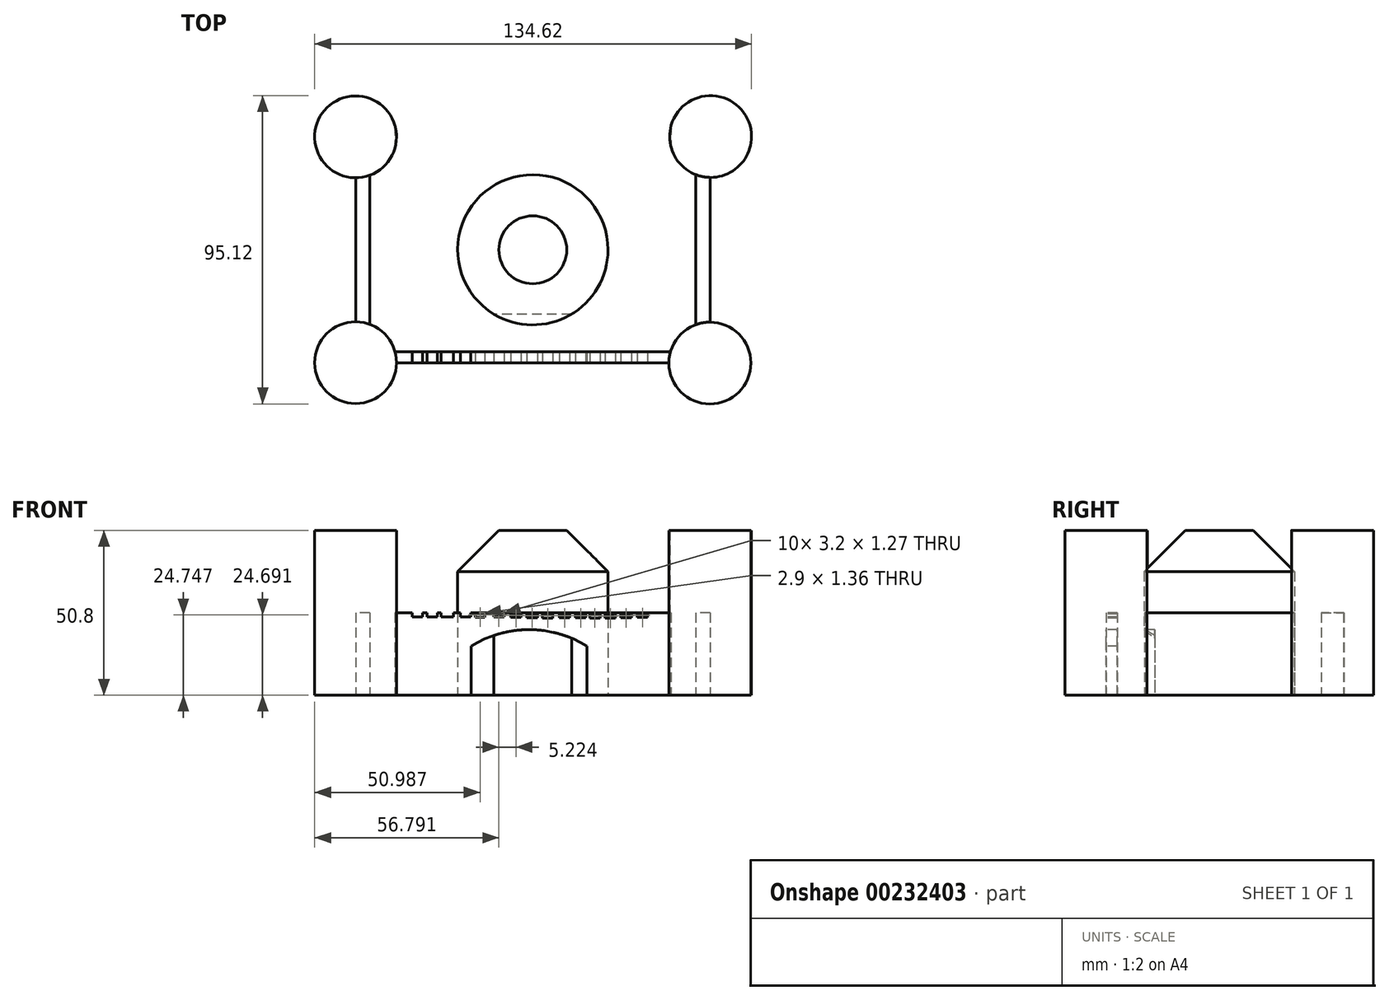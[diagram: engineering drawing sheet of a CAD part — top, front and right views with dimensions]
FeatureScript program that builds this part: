
annotation { "Feature Type Name" : "Feature", "Feature Type Description" : "" }
export const myFeature = defineFeature(function(context is Context, id is Id, definition is map)
    precondition{}
    {
        {
            var Q0;
            Q0=qCreatedBy(makeId("Top.planeOp"),FACE);
            var sketch = newSketch(context, id + "F0", { "sketchPlane" : qUnion([Q0])});
            skLineSegment(sketch, "E0.bottom", {"start": v(41.96, -34.83) * mm, "end": v(-42, -34.83) * mm});
            skLineSegment(sketch, "E0.top", {"start": v(42.17, 34.83) * mm, "end": v(-42, 34.83) * mm});
            skLineSegment(sketch, "E0.left", {"start": v(54.6, -22.32) * mm, "end": v(54.6, 22.32) * mm});
            skLineSegment(sketch, "E0.right", {"start": v(-54.6, -34.83) * mm, "end": v(-54.6, -34.83) * mm});
            skPoint(sketch, "E0.middle", {"position": v(0, 0) * mm});
            skCircle(sketch, "E1", {"center": v(0, 0) * mm, "radius": 23.17 * mm});
            skCircle(sketch, "E2", {"center": v(-54.6, 34.83) * mm, "radius": 12.62 * mm});
            skCircle(sketch, "E3", {"center": v(54.79, 34.94) * mm, "radius": 12.62 * mm});
            skCircle(sketch, "E4", {"center": v(54.58, -34.94) * mm, "radius": 12.62 * mm});
            skCircle(sketch, "E5", {"center": v(-54.6, -34.83) * mm, "radius": 12.62 * mm});
            skLineSegment(sketch, "E6.bottom", {"start": v(42.46, -31.43) * mm, "end": v(-42.46, -31.43) * mm});
            skLineSegment(sketch, "E6.top", {"start": v(42.67, 31.43) * mm, "end": v(-42.46, 31.43) * mm});
            skLineSegment(sketch, "E6.left", {"start": v(50.25, -23.1) * mm, "end": v(50.25, 23.17) * mm});
            skLineSegment(sketch, "E6.right", {"start": v(-50.25, -23) * mm, "end": v(-50.25, 23) * mm});
            skPoint(sketch, "E7.orphan", {"position": v(54.6, 34.83) * mm});
            skLineSegment(sketch, "E8.trimOffspring", {"start": v(-54.6, -22.22) * mm, "end": v(-54.6, 22.22) * mm});
            skPoint(sketch, "E9.orphan", {"position": v(54.6, -34.83) * mm});
            skPoint(sketch, "E10.orphan", {"position": v(50.25, 31.43) * mm});
            skPoint(sketch, "E11.orphan", {"position": v(50.25, -31.43) * mm});
            skPoint(sketch, "E12.orphan", {"position": v(-50.25, -31.43) * mm});
            skPoint(sketch, "E13.orphan", {"position": v(-50.25, 31.43) * mm});
            skPoint(sketch, "E14.left.end.orphan", {"position": v(7.55, 3.82) * mm});
            skPoint(sketch, "E14.bottom.start.orphan", {"position": v(7.55, -3.82) * mm});
            skPoint(sketch, "E14.right.end.orphan", {"position": v(-7.55, 3.82) * mm});
            skPoint(sketch, "E14.right.start.orphan", {"position": v(-7.55, -3.82) * mm});
            skSolve(sketch);
        }
        {
            var Q0;
            {var subQ0=sQuery(id+"F0.wireOp",EDGE,"E0.top");Q0=makeQuery(id+"F0.imprint","IMPRINT",FACE,{"disambiguationData":[TD([[makeQuery(id+"F0.imprint","IMPRINT",EDGE,{"derivedFrom":subQ0}),1.0]])]});}
            var Q1;
            {var subQ0=sQuery(id+"F0.wireOp",EDGE,"E6.right");Q1=makeQuery(id+"F0.imprint","IMPRINT",FACE,{"disambiguationData":[TD([[makeQuery(id+"F0.imprint","IMPRINT",EDGE,{"derivedFrom":subQ0}),1.0]])]});}
            var Q2;
            {var subQ0=sQuery(id+"F0.wireOp",EDGE,"E0.bottom");Q2=makeQuery(id+"F0.imprint","IMPRINT",FACE,{"disambiguationData":[TD([[makeQuery(id+"F0.imprint","IMPRINT",EDGE,{"derivedFrom":subQ0}),-1.0]])]});}
            var Q3;
            {var subQ0=sQuery(id+"F0.wireOp",EDGE,"E0.left");Q3=makeQuery(id+"F0.imprint","IMPRINT",FACE,{"disambiguationData":[TD([[makeQuery(id+"F0.imprint","IMPRINT",EDGE,{"derivedFrom":subQ0}),1.0]])]});}
            extrude(context, id + "F1", {"entities" : qUnion([Q0, Q1, Q2, Q3]), "depth" : 25.4 * mm});
        }
        {
            var Q0;
            {var subQ0=sQuery(id+"F0.wireOp",EDGE,"E2");var subQ1=makeQuery(id+"F0.imprint","INTERSECT",VERTEX,{"derivedFrom":[sQuery(id+"F0.wireOp",EDGE,"E0.top"),subQ0]});Q0=makeQuery(id+"F0.imprint","IMPRINT",FACE,{"disambiguationData":[TD([[makeQuery(id+"F0.imprint","IMPRINT",EDGE,{"disambiguationData":[TD([[subQ1,-1.0]])],"derivedFrom":subQ0}),1.0]])]});}
            var Q1;
            {var subQ0=sQuery(id+"F0.wireOp",EDGE,"E3");var subQ1=makeQuery(id+"F0.imprint","INTERSECT",VERTEX,{"derivedFrom":[sQuery(id+"F0.wireOp",EDGE,"E0.top"),subQ0]});Q1=makeQuery(id+"F0.imprint","IMPRINT",FACE,{"disambiguationData":[TD([[makeQuery(id+"F0.imprint","IMPRINT",EDGE,{"disambiguationData":[TD([[subQ1,-1.0]])],"derivedFrom":subQ0}),1.0]])]});}
            var Q2;
            {var subQ0=sQuery(id+"F0.wireOp",EDGE,"E4");var subQ1=makeQuery(id+"F0.imprint","INTERSECT",VERTEX,{"derivedFrom":[sQuery(id+"F0.wireOp",EDGE,"E0.left"),subQ0]});Q2=makeQuery(id+"F0.imprint","IMPRINT",FACE,{"disambiguationData":[TD([[makeQuery(id+"F0.imprint","IMPRINT",EDGE,{"disambiguationData":[TD([[subQ1,-1.0]])],"derivedFrom":subQ0}),1.0]])]});}
            var Q3;
            {var subQ0=sQuery(id+"F0.wireOp",EDGE,"E5");var subQ1=makeQuery(id+"F0.imprint","INTERSECT",VERTEX,{"derivedFrom":[subQ0,sQuery(id+"F0.wireOp",EDGE,"E6.bottom")]});Q3=makeQuery(id+"F0.imprint","IMPRINT",FACE,{"disambiguationData":[TD([[makeQuery(id+"F0.imprint","IMPRINT",EDGE,{"disambiguationData":[TD([[subQ1,-1.0]])],"derivedFrom":subQ0}),1.0]])]});}
            var Q4;
            Q4=makeQuery(id+"F0.imprint","IMPRINT",FACE,{"disambiguationData":[TD([[makeQuery(id+"F0.imprint","IMPRINT",EDGE,{"derivedFrom":sQuery(id+"F0.wireOp",EDGE,"E1")}),1.0]])]});
            extrude(context, id + "F2", {"entities" : qUnion([Q0, Q1, Q2, Q3, Q4]), "depth" : 50.8 * mm});
        }
        {
            var Q0;
            Q0=makeQuery(id+"F1.opExtrude","SWEPT_FACE",FACE,{"disambiguationData":[OSD([sQuery(id+"F0.wireOp",EDGE,"E0.bottom")])]});
            var sketch = newSketch(context, id + "F3", { "sketchPlane" : qUnion([Q0])});
            skLineSegment(sketch, "E15.bottom", {"start": v(-19.02, 0) * mm, "end": v(16.75, 0) * mm});
            skLineSegment(sketch, "E15.left", {"start": v(-19.02, 0) * mm, "end": v(-19.02, 15.1) * mm});
            skLineSegment(sketch, "E15.right", {"start": v(16.75, 0) * mm, "end": v(16.75, 15.1) * mm});
            skArc(sketch, "E16", {"start": v(16.75, 15.1) * mm, "mid": v(-1.14, 20.2) * mm, "end": v(-19.02, 15.1) * mm});
            skSolve(sketch);
        }
        {
            var Q0;
            Q0=makeQuery(id+"F3.imprint","IMPRINT",FACE,{"disambiguationData":[TD([[makeQuery(id+"F3.imprint","IMPRINT",EDGE,{"derivedFrom":sQuery(id+"F3.wireOp",EDGE,"E15.bottom")}),-1.0]])]});
            extrude(context, id + "F4", {"entities" : qUnion([Q0]), "operationType" : NewBodyOperationType.REMOVE, "oppositeDirection" : true, "depth" : 15 * mm});
        }
        {
            var Q0;
            Q0=makeQuery(id+"F1.opExtrude","SWEPT_FACE",FACE,{"disambiguationData":[OSD([sQuery(id+"F0.wireOp",EDGE,"E0.bottom")])]});
            var sketch = newSketch(context, id + "F5", { "sketchPlane" : qUnion([Q0])});
            skLineSegment(sketch, "E17.bottom", {"start": v(-37.18, 25.4) * mm, "end": v(-33.98, 25.4) * mm});
            skLineSegment(sketch, "E17.top", {"start": v(-37.18, 24.13) * mm, "end": v(-33.98, 24.13) * mm});
            skLineSegment(sketch, "E17.left", {"start": v(-37.18, 25.4) * mm, "end": v(-37.18, 24.13) * mm});
            skLineSegment(sketch, "E17.right", {"start": v(-33.98, 25.4) * mm, "end": v(-33.98, 24.13) * mm});
            skLineSegment(sketch, "E18.bottom", {"start": v(-32.57, 25.42) * mm, "end": v(-29.37, 25.42) * mm});
            skLineSegment(sketch, "E18.top", {"start": v(-32.57, 24.15) * mm, "end": v(-29.37, 24.15) * mm});
            skLineSegment(sketch, "E18.left", {"start": v(-32.57, 25.42) * mm, "end": v(-32.57, 24.15) * mm});
            skLineSegment(sketch, "E18.right", {"start": v(-29.37, 25.42) * mm, "end": v(-29.37, 24.15) * mm});
            skLineSegment(sketch, "E19.bottom", {"start": v(-28.2, 25.5) * mm, "end": v(-24.42, 25.5) * mm});
            skLineSegment(sketch, "E19.top", {"start": v(-28.2, 24.08) * mm, "end": v(-24.42, 24.08) * mm});
            skLineSegment(sketch, "E19.left", {"start": v(-28.2, 25.5) * mm, "end": v(-28.2, 24.08) * mm});
            skLineSegment(sketch, "E19.right", {"start": v(-24.42, 25.5) * mm, "end": v(-24.42, 24.08) * mm});
            skLineSegment(sketch, "E20.bottom", {"start": v(-22.36, 25.45) * mm, "end": v(-19.15, 25.45) * mm});
            skLineSegment(sketch, "E20.top", {"start": v(-22.36, 24.18) * mm, "end": v(-19.15, 24.18) * mm});
            skLineSegment(sketch, "E20.left", {"start": v(-22.36, 25.45) * mm, "end": v(-22.36, 24.18) * mm});
            skLineSegment(sketch, "E20.right", {"start": v(-19.15, 25.45) * mm, "end": v(-19.15, 24.18) * mm});
            skLineSegment(sketch, "E21.bottom", {"start": v(-17.68, 25.37) * mm, "end": v(-14.78, 25.37) * mm});
            skLineSegment(sketch, "E21.top", {"start": v(-17.68, 24) * mm, "end": v(-14.78, 24) * mm});
            skLineSegment(sketch, "E21.left", {"start": v(-17.68, 25.37) * mm, "end": v(-17.68, 24) * mm});
            skLineSegment(sketch, "E21.right", {"start": v(-14.78, 25.37) * mm, "end": v(-14.78, 24) * mm});
            skLineSegment(sketch, "E22.bottom", {"start": v(-12.03, 25.38) * mm, "end": v(-8.83, 25.38) * mm});
            skLineSegment(sketch, "E22.top", {"start": v(-12.03, 24.11) * mm, "end": v(-8.83, 24.11) * mm});
            skLineSegment(sketch, "E22.left", {"start": v(-12.03, 25.38) * mm, "end": v(-12.03, 24.11) * mm});
            skLineSegment(sketch, "E22.right", {"start": v(-8.83, 25.38) * mm, "end": v(-8.83, 24.11) * mm});
            skLineSegment(sketch, "E23.bottom", {"start": v(-6.8, 25.2) * mm, "end": v(-3.6, 25.2) * mm});
            skLineSegment(sketch, "E23.top", {"start": v(-6.8, 23.93) * mm, "end": v(-3.6, 23.93) * mm});
            skLineSegment(sketch, "E23.left", {"start": v(-6.8, 25.2) * mm, "end": v(-6.8, 23.93) * mm});
            skLineSegment(sketch, "E23.right", {"start": v(-3.6, 25.2) * mm, "end": v(-3.6, 23.93) * mm});
            skLineSegment(sketch, "E24.bottom", {"start": v(-1.79, 25.14) * mm, "end": v(1.41, 25.14) * mm});
            skLineSegment(sketch, "E24.top", {"start": v(-1.79, 23.86) * mm, "end": v(1.41, 23.86) * mm});
            skLineSegment(sketch, "E24.left", {"start": v(-1.79, 25.14) * mm, "end": v(-1.79, 23.86) * mm});
            skLineSegment(sketch, "E24.right", {"start": v(1.41, 25.14) * mm, "end": v(1.41, 23.86) * mm});
            skLineSegment(sketch, "E25.bottom", {"start": v(3, 25.07) * mm, "end": v(6.2, 25.07) * mm});
            skLineSegment(sketch, "E25.top", {"start": v(3, 23.8) * mm, "end": v(6.2, 23.8) * mm});
            skLineSegment(sketch, "E25.left", {"start": v(3, 25.07) * mm, "end": v(3, 23.8) * mm});
            skLineSegment(sketch, "E25.right", {"start": v(6.2, 25.07) * mm, "end": v(6.2, 23.8) * mm});
            skLineSegment(sketch, "E26.bottom", {"start": v(8.18, 25.12) * mm, "end": v(11.39, 25.12) * mm});
            skLineSegment(sketch, "E26.top", {"start": v(8.18, 23.85) * mm, "end": v(11.39, 23.85) * mm});
            skLineSegment(sketch, "E26.left", {"start": v(8.18, 25.12) * mm, "end": v(8.18, 23.85) * mm});
            skLineSegment(sketch, "E26.right", {"start": v(11.39, 25.12) * mm, "end": v(11.39, 23.85) * mm});
            skLineSegment(sketch, "E27.bottom", {"start": v(13.16, 25.12) * mm, "end": v(16.36, 25.12) * mm});
            skLineSegment(sketch, "E27.top", {"start": v(13.16, 23.85) * mm, "end": v(16.36, 23.85) * mm});
            skLineSegment(sketch, "E27.left", {"start": v(13.16, 25.12) * mm, "end": v(13.16, 23.85) * mm});
            skLineSegment(sketch, "E27.right", {"start": v(16.36, 25.12) * mm, "end": v(16.36, 23.85) * mm});
            skLineSegment(sketch, "E28.bottom", {"start": v(17.54, 25.07) * mm, "end": v(20.75, 25.07) * mm});
            skLineSegment(sketch, "E28.top", {"start": v(17.54, 23.8) * mm, "end": v(20.75, 23.8) * mm});
            skLineSegment(sketch, "E28.left", {"start": v(17.54, 25.07) * mm, "end": v(17.54, 23.8) * mm});
            skLineSegment(sketch, "E28.right", {"start": v(20.75, 25.07) * mm, "end": v(20.75, 23.8) * mm});
            skLineSegment(sketch, "E29.bottom", {"start": v(22.3, 25.01) * mm, "end": v(25.5, 25.01) * mm});
            skLineSegment(sketch, "E29.top", {"start": v(22.3, 23.74) * mm, "end": v(25.5, 23.74) * mm});
            skLineSegment(sketch, "E29.left", {"start": v(22.3, 25.01) * mm, "end": v(22.3, 23.74) * mm});
            skLineSegment(sketch, "E29.right", {"start": v(25.5, 25.01) * mm, "end": v(25.5, 23.74) * mm});
            skLineSegment(sketch, "E30.bottom", {"start": v(27.15, 25.1) * mm, "end": v(30.36, 25.1) * mm});
            skLineSegment(sketch, "E30.top", {"start": v(27.15, 23.82) * mm, "end": v(30.36, 23.82) * mm});
            skLineSegment(sketch, "E30.left", {"start": v(27.15, 25.1) * mm, "end": v(27.15, 23.82) * mm});
            skLineSegment(sketch, "E30.right", {"start": v(30.36, 25.1) * mm, "end": v(30.36, 23.82) * mm});
            skLineSegment(sketch, "E31.bottom", {"start": v(32.18, 25.2) * mm, "end": v(35.39, 25.2) * mm});
            skLineSegment(sketch, "E31.top", {"start": v(32.18, 23.93) * mm, "end": v(35.39, 23.93) * mm});
            skLineSegment(sketch, "E31.left", {"start": v(32.18, 25.2) * mm, "end": v(32.18, 23.93) * mm});
            skLineSegment(sketch, "E31.right", {"start": v(35.39, 25.2) * mm, "end": v(35.39, 23.93) * mm});
            skSolve(sketch);
        }
        {
            var Q0;
            Q0=makeQuery(id+"F5.imprint","IMPRINT",FACE,{"disambiguationData":[TD([[makeQuery(id+"F5.imprint","IMPRINT",EDGE,{"derivedFrom":sQuery(id+"F5.wireOp",EDGE,"E17.bottom")}),1.0]])]});
            var Q1;
            {var subQ0=sQuery(id+"F5.wireOp",EDGE,"E18.top");Q1=makeQuery(id+"F5.imprint","IMPRINT",FACE,{"disambiguationData":[TD([[makeQuery(id+"F5.imprint","IMPRINT",EDGE,{"derivedFrom":subQ0}),1.0]])]});}
            var Q2;
            {var subQ0=sQuery(id+"F5.wireOp",EDGE,"E19.top");Q2=makeQuery(id+"F5.imprint","IMPRINT",FACE,{"disambiguationData":[TD([[makeQuery(id+"F5.imprint","IMPRINT",EDGE,{"derivedFrom":subQ0}),1.0]])]});}
            var Q3;
            {var subQ0=sQuery(id+"F5.wireOp",EDGE,"E20.top");Q3=makeQuery(id+"F5.imprint","IMPRINT",FACE,{"disambiguationData":[TD([[makeQuery(id+"F5.imprint","IMPRINT",EDGE,{"derivedFrom":subQ0}),1.0]])]});}
            var Q4;
            Q4=makeQuery(id+"F5.imprint","IMPRINT",FACE,{"disambiguationData":[TD([[makeQuery(id+"F5.imprint","IMPRINT",EDGE,{"derivedFrom":sQuery(id+"F5.wireOp",EDGE,"E21.bottom")}),-1.0]])]});
            var Q5;
            Q5=makeQuery(id+"F5.imprint","IMPRINT",FACE,{"disambiguationData":[TD([[makeQuery(id+"F5.imprint","IMPRINT",EDGE,{"derivedFrom":sQuery(id+"F5.wireOp",EDGE,"E22.bottom")}),-1.0]])]});
            var Q6;
            Q6=makeQuery(id+"F5.imprint","IMPRINT",FACE,{"disambiguationData":[TD([[makeQuery(id+"F5.imprint","IMPRINT",EDGE,{"derivedFrom":sQuery(id+"F5.wireOp",EDGE,"E23.bottom")}),-1.0]])]});
            var Q7;
            Q7=makeQuery(id+"F5.imprint","IMPRINT",FACE,{"disambiguationData":[TD([[makeQuery(id+"F5.imprint","IMPRINT",EDGE,{"derivedFrom":sQuery(id+"F5.wireOp",EDGE,"E24.bottom")}),-1.0]])]});
            var Q8;
            Q8=makeQuery(id+"F5.imprint","IMPRINT",FACE,{"disambiguationData":[TD([[makeQuery(id+"F5.imprint","IMPRINT",EDGE,{"derivedFrom":sQuery(id+"F5.wireOp",EDGE,"E25.bottom")}),-1.0]])]});
            var Q9;
            Q9=makeQuery(id+"F5.imprint","IMPRINT",FACE,{"disambiguationData":[TD([[makeQuery(id+"F5.imprint","IMPRINT",EDGE,{"derivedFrom":sQuery(id+"F5.wireOp",EDGE,"E26.bottom")}),-1.0]])]});
            var Q10;
            Q10=makeQuery(id+"F5.imprint","IMPRINT",FACE,{"disambiguationData":[TD([[makeQuery(id+"F5.imprint","IMPRINT",EDGE,{"derivedFrom":sQuery(id+"F5.wireOp",EDGE,"E27.bottom")}),-1.0]])]});
            var Q11;
            Q11=makeQuery(id+"F5.imprint","IMPRINT",FACE,{"disambiguationData":[TD([[makeQuery(id+"F5.imprint","IMPRINT",EDGE,{"derivedFrom":sQuery(id+"F5.wireOp",EDGE,"E28.bottom")}),-1.0]])]});
            var Q12;
            Q12=makeQuery(id+"F5.imprint","IMPRINT",FACE,{"disambiguationData":[TD([[makeQuery(id+"F5.imprint","IMPRINT",EDGE,{"derivedFrom":sQuery(id+"F5.wireOp",EDGE,"E29.bottom")}),-1.0]])]});
            var Q13;
            Q13=makeQuery(id+"F5.imprint","IMPRINT",FACE,{"disambiguationData":[TD([[makeQuery(id+"F5.imprint","IMPRINT",EDGE,{"derivedFrom":sQuery(id+"F5.wireOp",EDGE,"E30.bottom")}),-1.0]])]});
            var Q14;
            Q14=makeQuery(id+"F5.imprint","IMPRINT",FACE,{"disambiguationData":[TD([[makeQuery(id+"F5.imprint","IMPRINT",EDGE,{"derivedFrom":sQuery(id+"F5.wireOp",EDGE,"E31.bottom")}),-1.0]])]});
            var Q15;
            Q15=makeQuery(id+"F1.opExtrude","SWEPT_FACE",FACE,{"disambiguationData":[OSD([sQuery(id+"F0.wireOp",EDGE,"E6.top")])]});
            var Q16;
            Q16=makeQuery(id+"F1.opExtrude","SWEPT_FACE",FACE,{"disambiguationData":[OSD([sQuery(id+"F0.wireOp",EDGE,"E0.top")])]});
            extrude(context, id + "F6", {"entities" : qUnion([Q0, Q1, Q2, Q3, Q4, Q5, Q6, Q7, Q8, Q9, Q10, Q11, Q12, Q13, Q14, Q15, Q16]), "operationType" : NewBodyOperationType.REMOVE, "oppositeDirection" : true, "depth" : 7.11 * mm});
        }
        {
            var Q0;
            Q0=makeQuery(id+"F2.opExtrude","CAP_EDGE",EDGE,{"disambiguationData":[OSD([sQuery(id+"F0.wireOp",EDGE,"E1")])],"isStart":false});
            chamfer(context, id + "F7", {"entities" : qUnion([Q0]), "width" : 12.7 * mm, "tangentPropagation" : true});
        }
    });
